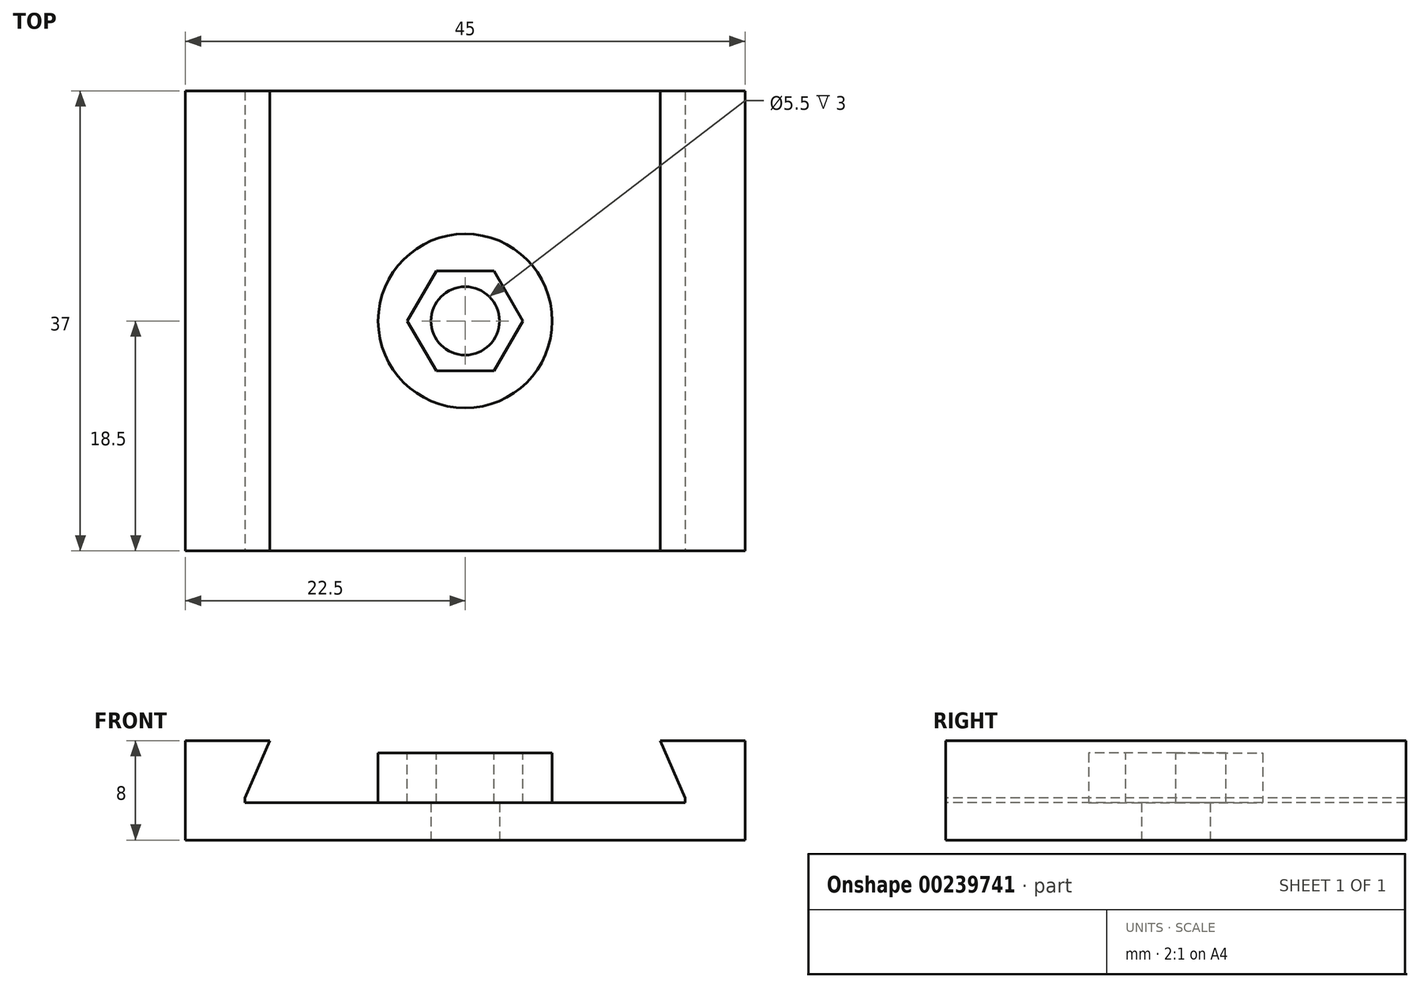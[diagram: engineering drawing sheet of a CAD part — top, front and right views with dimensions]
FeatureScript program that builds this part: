
annotation { "Feature Type Name" : "Feature", "Feature Type Description" : "" }
export const myFeature = defineFeature(function(context is Context, id is Id, definition is map)
    precondition{}
    {
        {
            var Q0;
            Q0=qCreatedBy(makeId("Top.planeOp"),FACE);
            var sketch = newSketch(context, id + "F0", { "sketchPlane" : qUnion([Q0])});
            skLineSegment(sketch, "E0.bottom", {"start": v(22.5, -18.5) * mm, "end": v(-22.5, -18.5) * mm});
            skLineSegment(sketch, "E0.top", {"start": v(22.5, 18.5) * mm, "end": v(-22.5, 18.5) * mm});
            skLineSegment(sketch, "E0.left", {"start": v(22.5, -18.5) * mm, "end": v(22.5, 18.5) * mm});
            skLineSegment(sketch, "E0.right", {"start": v(-22.5, -18.5) * mm, "end": v(-22.5, 18.5) * mm});
            skPoint(sketch, "E0.middle", {"position": v(0, 0) * mm});
            skSolve(sketch);
        }
        {
            var Q0;
            Q0=qSketchRegion(id+"F0",true);
            extrude(context, id + "F1", {"entities" : qUnion([Q0]), "depth" : 8 * mm});
        }
        {
            var Q0;
            Q0=makeQuery(id+"F1.opExtrude","SWEPT_FACE",FACE,{"disambiguationData":[OSD([sQuery(id+"F0.wireOp",EDGE,"E0.bottom")])]});
            var sketch = newSketch(context, id + "F2", { "sketchPlane" : qUnion([Q0])});
            skLineSegment(sketch, "E1", {"start": v(-22.5, 3) * mm, "end": v(22.5, 3) * mm, "construction": true});
            skLineSegment(sketch, "E2", {"start": v(-17.7, 8) * mm, "end": v(-17.7, 0) * mm, "construction": true});
            skLineSegment(sketch, "E3", {"start": v(0, 13.1) * mm, "end": v(0, -6.27) * mm, "construction": true});
            skLineSegment(sketch, "E4.MirrorCS", {"start": v(17.7, 8) * mm, "end": v(17.7, 0) * mm, "construction": true});
            skLineSegment(sketch, "E5", {"start": v(-15.7, 8) * mm, "end": v(-15.7, 0) * mm, "construction": true});
            skLineSegment(sketch, "E6", {"start": v(-15.7, 8) * mm, "end": v(15.7, 8) * mm});
            skLineSegment(sketch, "E7", {"start": v(-17.7, 3) * mm, "end": v(17.7, 3) * mm});
            skLineSegment(sketch, "E8", {"start": v(-17.7, 3) * mm, "end": v(-17.7, 3.4) * mm});
            skLineSegment(sketch, "E9", {"start": v(-17.7, 3.4) * mm, "end": v(-15.7, 8) * mm});
            skLineSegment(sketch, "E10.MirrorCS", {"start": v(17.7, 3.4) * mm, "end": v(15.7, 8) * mm});
            skLineSegment(sketch, "E11", {"start": v(17.7, 3.4) * mm, "end": v(17.7, 3) * mm});
            skSolve(sketch);
        }
        {
            var Q0;
            Q0=qSketchRegion(id+"F2",true);
            extrude(context, id + "F3", {"entities" : qUnion([Q0]), "operationType" : NewBodyOperationType.REMOVE, "endBound" : BoundingType.THROUGH_ALL, "oppositeDirection" : true, "depth" : 25 * mm});
        }
        {
            var Q0;
            Q0=makeQuery(id+"F1.opExtrude","CAP_FACE",FACE,{"disambiguationData":[OSD([sQuery(id+"F0.wireOp",EDGE,"E0.bottom"),sQuery(id+"F0.wireOp",EDGE,"E0.top"),sQuery(id+"F0.wireOp",EDGE,"E0.left"),sQuery(id+"F0.wireOp",EDGE,"E0.right")])],"isStart":true});
            var sketch = newSketch(context, id + "F4", { "sketchPlane" : qUnion([Q0])});
            skCircle(sketch, "E12", {"center": v(0, 0) * mm, "radius": 2.75 * mm});
            skSolve(sketch);
        }
        {
            var Q0;
            Q0=makeQuery(id+"F3.boolean.opBoolean","COPY",FACE,{"derivedFrom":makeQuery(id+"F3.opExtrude","SWEPT_FACE",FACE,{"disambiguationData":[OSD([sQuery(id+"F2.wireOp",EDGE,"E7")])]})});
            var sketch = newSketch(context, id + "F5", { "sketchPlane" : qUnion([Q0])});
            skCircle(sketch, "E13", {"center": v(0, 0) * mm, "radius": 7 * mm});
            skSolve(sketch);
        }
        {
            var Q0;
            Q0=qSketchRegion(id+"F5",true);
            extrude(context, id + "F6", {"entities" : qUnion([Q0]), "operationType" : NewBodyOperationType.ADD, "depth" : 4 * mm});
        }
        {
            var Q0;
            Q0=qSketchRegion(id+"F4",true);
            extrude(context, id + "F7", {"entities" : qUnion([Q0]), "operationType" : NewBodyOperationType.REMOVE, "oppositeDirection" : true, "depth" : 25 * mm});
        }
        {
            var Q0;
            Q0=makeQuery(id+"F6.opExtrude","CAP_FACE",FACE,{"disambiguationData":[OSD([sQuery(id+"F5.wireOp",EDGE,"E13")])],"isStart":false});
            var sketch = newSketch(context, id + "F8", { "sketchPlane" : qUnion([Q0])});
            skCircle(sketch, "E14.cCircle", {"center": v(0, 0) * mm, "radius": 4.65 * mm, "construction": true});
            skLineSegment(sketch, "E14.0", {"start": v(4.65, 0) * mm, "end": v(2.33, -4.03) * mm});
            skLineSegment(sketch, "E14.1", {"start": v(2.32, -4.03) * mm, "end": v(-2.32, -4.03) * mm});
            skLineSegment(sketch, "E14.2", {"start": v(-2.32, -4.03) * mm, "end": v(-4.65, 0) * mm});
            skLineSegment(sketch, "E14.3", {"start": v(-4.65, 0) * mm, "end": v(-2.33, 4.03) * mm});
            skLineSegment(sketch, "E14.4", {"start": v(-2.33, 4.03) * mm, "end": v(2.32, 4.03) * mm});
            skLineSegment(sketch, "E14.5", {"start": v(2.32, 4.03) * mm, "end": v(4.65, 0) * mm});
            skSolve(sketch);
        }
        {
            var Q0;
            Q0=makeQuery(id+"F8.imprint","IMPRINT",FACE,{"disambiguationData":[TD([[makeQuery(id+"F8.imprint","IMPRINT",EDGE,{"derivedFrom":sQuery(id+"F8.wireOp",EDGE,"E14.0")}),-1.0]])]});
            extrude(context, id + "F9", {"entities" : qUnion([Q0]), "operationType" : NewBodyOperationType.REMOVE, "oppositeDirection" : true, "depth" : 4 * mm});
        }
    });
